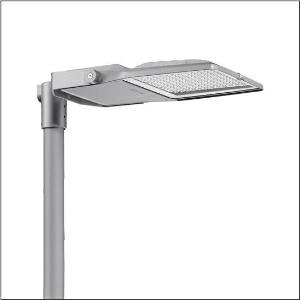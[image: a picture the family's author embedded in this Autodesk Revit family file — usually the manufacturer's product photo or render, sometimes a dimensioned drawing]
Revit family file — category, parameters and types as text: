
# Revit family: floodlight_fl_21_iq_midi___pl43_5xa7781e2a3a_1390
name_source: partatom
category: Lighting Fixtures
units: mm (PartAtom-declared; Revit-internal decimal feet)

## family parameters
Cut with Voids When Loaded = No
Host = Face
Light Source = No
Part Type = Normal
Room Calculation Point = No
Round Connector Dimension = Use Diameter
Shared = No

## types (1)
- --- (1 x LED, 27540 lm, 208.1 W, 3000K)
    Apparent Load = 208 VA
    CIE Flux Codes = 27 78 99 100 100
    Color Rendering = 70
    Color Temperature = 3000K
    Default Elevation = 1800 mm
    Description = Floodlight FL 21 iQ midi, floodlight, primary light control with lens, of PMMA, primary optical cover: protective disc, of toughened safety glass, transparent, light distribution: PL43, light emission: direct distribution, installation type: surface-mounted, LED, High Power LED, rated luminous flux: 27.540lm, luminous efficacy: 132lm/W, light colour: 730, colour temperature: 3000K, control gear: ECG iQ, control: optimised constant luminous flux control (CLO 2.0), Desk-Remote (wireless, voltage-free reading and setting of iQ features in the workshop via application-optimized NFC function/RFID function), Light-Fading, Smart-Wire, Night-Set, Lumen-Switch, Temp-Guard, Auto-Match, with terminal, 6-pole, mains connection: 220..240V, AC, 50/60Hz, start of lifetime: 208W, end of service life: 227W, reduction: 90W, luminaire housing, of diecast aluminium, powder-coated, Siteco® metallic grey (DB 702S), corrosivity category C5 mid according to DIN EN ISO 12944, sealing non-destructively replaceable, please order mast flange separately, mast bracket, of steel, galvanised, powder-coated, Siteco® metallic grey (DB 702S), protection rating (complete): IP66, insulation class (complete): insulation class II (safety insulation), certification: CE, protection symbol: D, impact resistance: IK08, permissible operating ambient temperature: -40..+40°C, permissible operating ambient temperature for outdoor applications: -40..+50°C, standard: DIN EN 12944, LABS conformity tested according to VDMA 24364:2018-05, packaging unit: 1 piece

Light Distribution: PL43
    Height = 76 mm
    Lamp = 1 x LED
    Lamp Light Flux = 27540 lm
    Lamp Power = 208.1 W
    Lamp count = 1
    Length = 657 mm
    Luminous efficacy = 132 lm/W
    Manufacturer = Siteco
    ModVariant = No
    Model = 5XA7781E2A3A
    Number of Poles = 1
    OnlyDefault = Yes
    Power Factor = 1
    Product Name = Floodlight FL 21 iQ midi | PL43
    Product group = floodlight | pylon annexe
    ProductGroupID = 6200
    Protection Class = Protection class II
    Protection Degree = IP 66
    RLX_Detail_Level = 1
    RLX_Emergency_Light_Flux = 0 lm
    RLX_Emergency_Type = 0
    RLX_Emergency_Type_DB = No
    RlxData = <blob elided: 153581 chars, md5=75690151>
    Socket = socket
    Standby Power = 0 W
    System Light Flux = 27540 lm
    System Power = 208 W
    Type Comments = factory setting: luminous flux: 100 % | dim-lin: 254 | 710 mA
    Type Image = l_1007123.jpg
    URL = http://relux.com
    VarID = @adj_035503
    Voltage = 0 V
    Weight = 0.00 kg
    Width = 442 mm

## geometry (parser evidence)
native form markers: Blend x4, Sweep x13
no freeform markers — native parametric forms only
